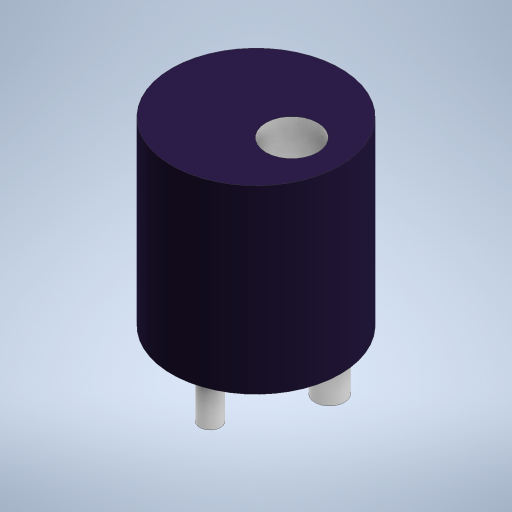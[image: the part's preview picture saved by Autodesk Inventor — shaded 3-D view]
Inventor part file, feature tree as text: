
AUTODESK INVENTOR PART (.ipt)
format: ipt  version: 2024 (Build 280153000, 153)  size: 236,032 bytes
history: native  units: mm
features: extrude x3, sketch x3
ambient origin geometry x8: Origin, YZ Plane, XZ Plane, XY Plane, X Axis, Y Axis, Z Axis, Center Point
bodies: Solid1 (feature_tree)
feature tree (6):
  extrude  "Extrusion1"  Depth=15.0mm TaperAngle=0.0deg
  extrude  "Extrusion2"  Depth=5.0mm TaperAngle=0.0deg
  extrude  "Extrusion3"  [1 undecoded]
  sketch  "Sketch1"  dims[d0=14.0mm d1=15.0mm d2=0.0mm]
  sketch  "Sketch2"  dims[d3=10.0mm d4=0.0mm d5=5.0mm d6=0.0mm]
  sketch  "Sketch3"
note: 1 required parameter value undecoded (feature->parameter linkage not recoverable at this tier; creation-order binding heuristic only, values carry confidence <= 0.55)
